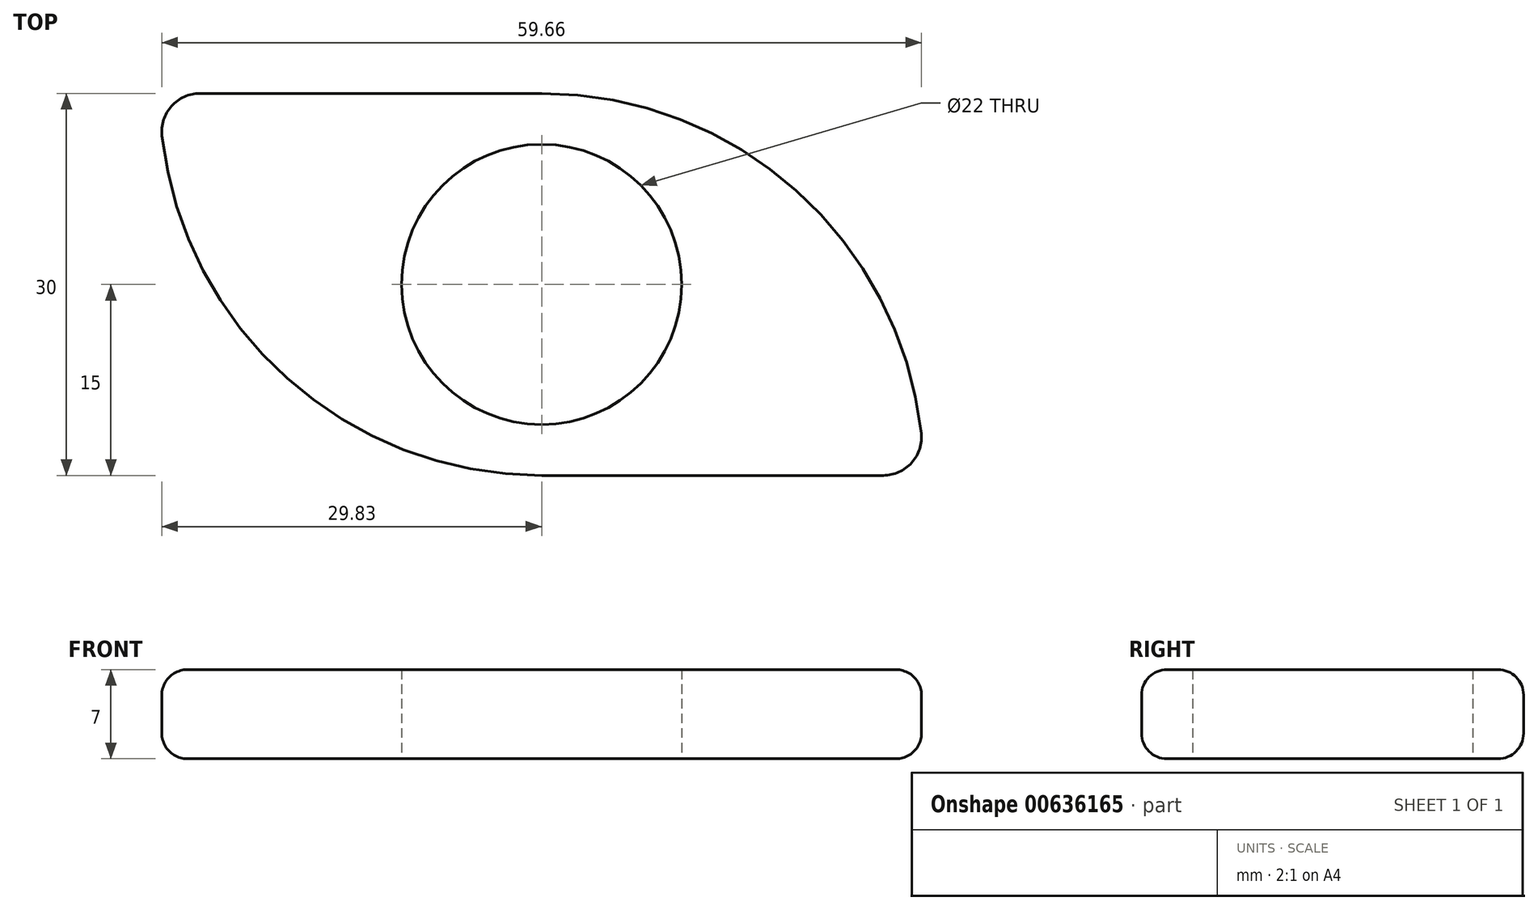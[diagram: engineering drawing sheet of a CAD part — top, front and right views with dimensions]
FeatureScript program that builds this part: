
annotation { "Feature Type Name" : "Feature", "Feature Type Description" : "" }
export const myFeature = defineFeature(function(context is Context, id is Id, definition is map)
    precondition{}
    {
        {
            var Q0;
            Q0=qCreatedBy(makeId("Top.planeOp"),FACE);
            var sketch = newSketch(context, id + "F0", { "sketchPlane" : qUnion([Q0])});
            skCircle(sketch, "E0", {"center": v(0, 0) * mm, "radius": 11 * mm});
            skLineSegment(sketch, "E1.bottom", {"start": v(30, 15) * mm, "end": v(-30, 15) * mm});
            skLineSegment(sketch, "E1.top", {"start": v(30, -15) * mm, "end": v(-30, -15) * mm});
            skLineSegment(sketch, "E1.left", {"start": v(30, 15) * mm, "end": v(30, -15) * mm});
            skLineSegment(sketch, "E1.right", {"start": v(-30, 15) * mm, "end": v(-30, -15) * mm});
            skSolve(sketch);
        }
        {
            var Q0;
            Q0 = qSketchRegion(id + "F0", true);
            extrude(context, id + "F1", {"entities" : qUnion([Q0]), "depth" : 7 * mm, "offsetDistance" : 25 * mm});
        }
        {
            var Q0;
            Q0=makeQuery(id+"F1.opExtrude","SWEPT_EDGE",EDGE,{"disambiguationData":[OSD([sQuery(id+"F0.wireOp",EDGE,"E1.top"),sQuery(id+"F0.wireOp",EDGE,"E1.right")])]});
            var Q1;
            Q1=makeQuery(id+"F1.opExtrude","SWEPT_EDGE",EDGE,{"disambiguationData":[OSD([sQuery(id+"F0.wireOp",EDGE,"E1.bottom"),sQuery(id+"F0.wireOp",EDGE,"E1.left")])]});
            fillet(context, id + "F2", {"entities" : qUnion([Q0, Q1]), "radius" : 30 * mm, "tangentPropagation" : true, "allowEdgeOverflow" : false});
        }
        {
            var Q0;
            Q0=makeQuery(id+"F2.opFillet","BLEND_EDGE",EDGE,{"blendedFrom":[makeQuery(id+"F1.opExtrude","SWEPT_EDGE",EDGE,{"disambiguationData":[OSD([sQuery(id+"F0.wireOp",EDGE,"E1.bottom"),sQuery(id+"F0.wireOp",EDGE,"E1.left")])]}),makeQuery(id+"F1.opExtrude","SWEPT_FACE",FACE,{"disambiguationData":[OSD([sQuery(id+"F0.wireOp",EDGE,"E1.top")])]})],"blendedInto":[makeQuery(id+"F1.opExtrude","SWEPT_FACE",FACE,{"disambiguationData":[OSD([sQuery(id+"F0.wireOp",EDGE,"E1.top")])]})]});
            var Q1;
            Q1=makeQuery(id+"F2.opFillet","BLEND_EDGE",EDGE,{"blendedFrom":[makeQuery(id+"F1.opExtrude","SWEPT_EDGE",EDGE,{"disambiguationData":[OSD([sQuery(id+"F0.wireOp",EDGE,"E1.top"),sQuery(id+"F0.wireOp",EDGE,"E1.right")])]}),makeQuery(id+"F1.opExtrude","SWEPT_FACE",FACE,{"disambiguationData":[OSD([sQuery(id+"F0.wireOp",EDGE,"E1.bottom")])]})],"blendedInto":[makeQuery(id+"F1.opExtrude","SWEPT_FACE",FACE,{"disambiguationData":[OSD([sQuery(id+"F0.wireOp",EDGE,"E1.bottom")])]})]});
            fillet(context, id + "F3", {"entities" : qUnion([Q0, Q1]), "radius" : 3 * mm, "tangentPropagation" : true, "allowEdgeOverflow" : false});
        }
        {
            var Q0;
            {var subQ0=sQuery(id+"F0.wireOp",EDGE,"E1.right");var subQ1=sQuery(id+"F0.wireOp",EDGE,"E1.top");Q0=makeQuery(id+"F2.opFillet","BLEND_EDGE",EDGE,{"blendedFrom":[makeQuery(id+"F1.opExtrude","SWEPT_EDGE",EDGE,{"disambiguationData":[OSD([subQ1,subQ0])]}),makeQuery(id+"F1.opExtrude","CAP_FACE",FACE,{"disambiguationData":[OSD([sQuery(id+"F0.wireOp",EDGE,"E0"),sQuery(id+"F0.wireOp",EDGE,"E1.bottom"),subQ1,sQuery(id+"F0.wireOp",EDGE,"E1.left"),subQ0])],"isStart":false})],"blendedInto":[makeQuery(id+"F1.opExtrude","CAP_FACE",FACE,{"disambiguationData":[OSD([sQuery(id+"F0.wireOp",EDGE,"E0"),sQuery(id+"F0.wireOp",EDGE,"E1.bottom"),subQ1,sQuery(id+"F0.wireOp",EDGE,"E1.left"),subQ0])],"isStart":false})]});}
            var Q1;
            {var subQ0=sQuery(id+"F0.wireOp",EDGE,"E1.right");var subQ1=sQuery(id+"F0.wireOp",EDGE,"E1.top");Q1=makeQuery(id+"F2.opFillet","BLEND_EDGE",EDGE,{"blendedFrom":[makeQuery(id+"F1.opExtrude","SWEPT_EDGE",EDGE,{"disambiguationData":[OSD([subQ1,subQ0])]}),makeQuery(id+"F1.opExtrude","CAP_FACE",FACE,{"disambiguationData":[OSD([sQuery(id+"F0.wireOp",EDGE,"E0"),sQuery(id+"F0.wireOp",EDGE,"E1.bottom"),subQ1,sQuery(id+"F0.wireOp",EDGE,"E1.left"),subQ0])],"isStart":true})],"blendedInto":[makeQuery(id+"F1.opExtrude","CAP_FACE",FACE,{"disambiguationData":[OSD([sQuery(id+"F0.wireOp",EDGE,"E0"),sQuery(id+"F0.wireOp",EDGE,"E1.bottom"),subQ1,sQuery(id+"F0.wireOp",EDGE,"E1.left"),subQ0])],"isStart":true})]});}
            fillet(context, id + "F4", {"entities" : qUnion([Q0, Q1]), "radius" : 2 * mm, "tangentPropagation" : true, "allowEdgeOverflow" : false});
        }
    });
